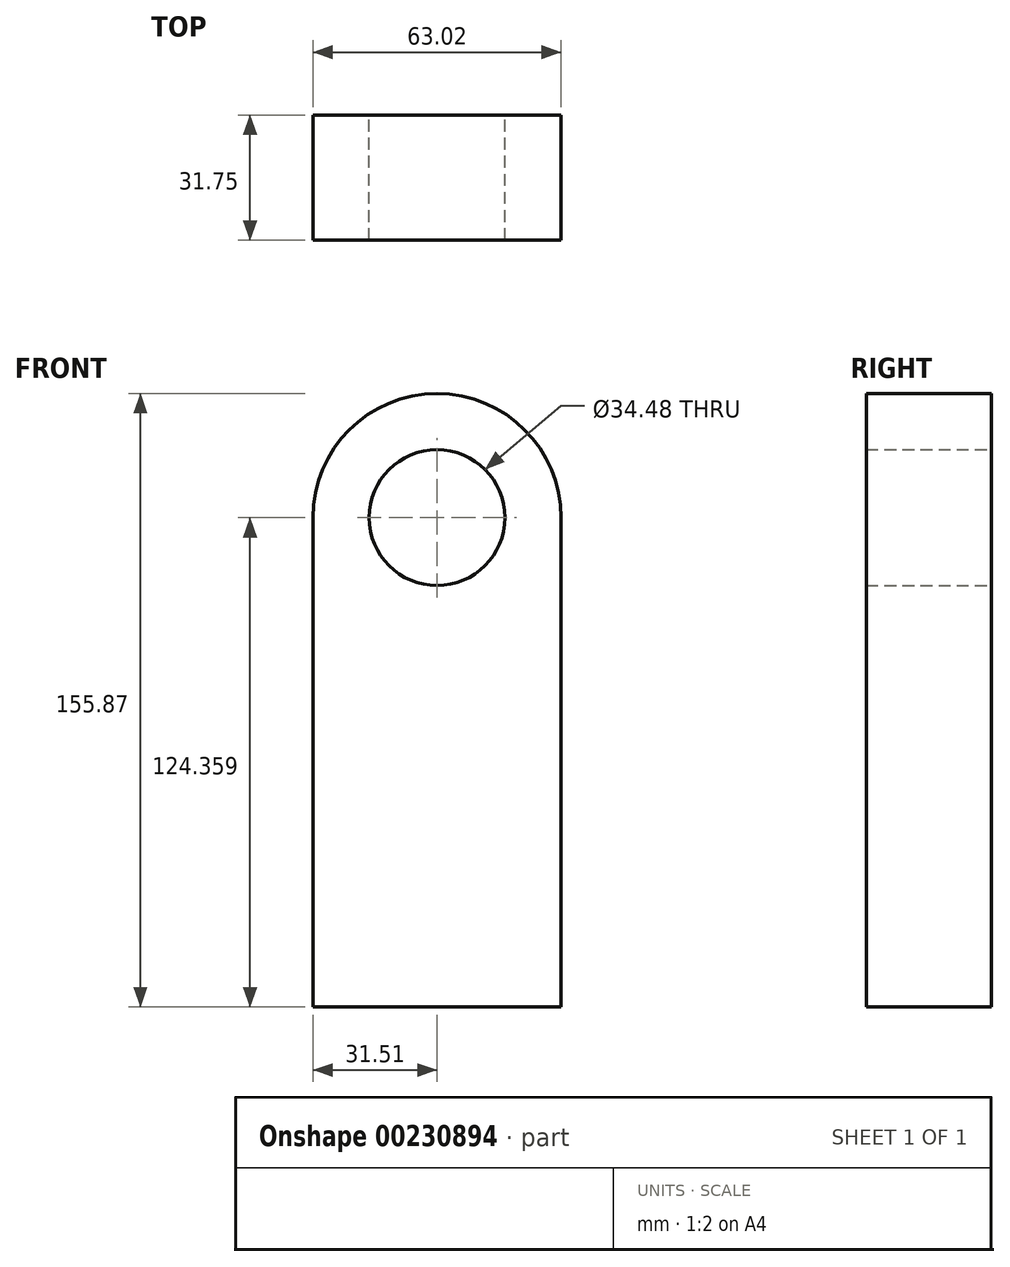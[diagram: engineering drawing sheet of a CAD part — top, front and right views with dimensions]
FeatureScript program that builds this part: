
annotation { "Feature Type Name" : "Feature", "Feature Type Description" : "" }
export const myFeature = defineFeature(function(context is Context, id is Id, definition is map)
    precondition{}
    {
        {
            var Q0;
            Q0=qCreatedBy(makeId("Front.planeOp"),FACE);
            var sketch = newSketch(context, id + "F0", { "sketchPlane" : qUnion([Q0])});
            skLineSegment(sketch, "E0.top", {"start": v(31.5, -62.18) * mm, "end": v(-31.5, -62.18) * mm});
            skLineSegment(sketch, "E0.left", {"start": v(31.5, 62.18) * mm, "end": v(31.5, -62.18) * mm});
            skLineSegment(sketch, "E0.right", {"start": v(-31.5, 62.18) * mm, "end": v(-31.5, -62.18) * mm});
            skPoint(sketch, "E0.middle", {"position": v(0, 0) * mm});
            skArc(sketch, "E1", {"start": v(31.5, 62.18) * mm, "mid": v(0, 93.69) * mm, "end": v(-31.5, 62.18) * mm});
            skCircle(sketch, "E2", {"center": v(0, 62.18) * mm, "radius": 17.24 * mm});
            skSolve(sketch);
        }
        {
            var Q0;
            Q0=makeQuery(id+"F0.imprint","IMPRINT",FACE,{"disambiguationData":[TD([[makeQuery(id+"F0.imprint","IMPRINT",EDGE,{"derivedFrom":sQuery(id+"F0.wireOp",EDGE,"E0.top")}),-1.0]])]});
            extrude(context, id + "F1", {"entities" : qUnion([Q0]), "depth" : 31.75 * mm});
        }
    });
